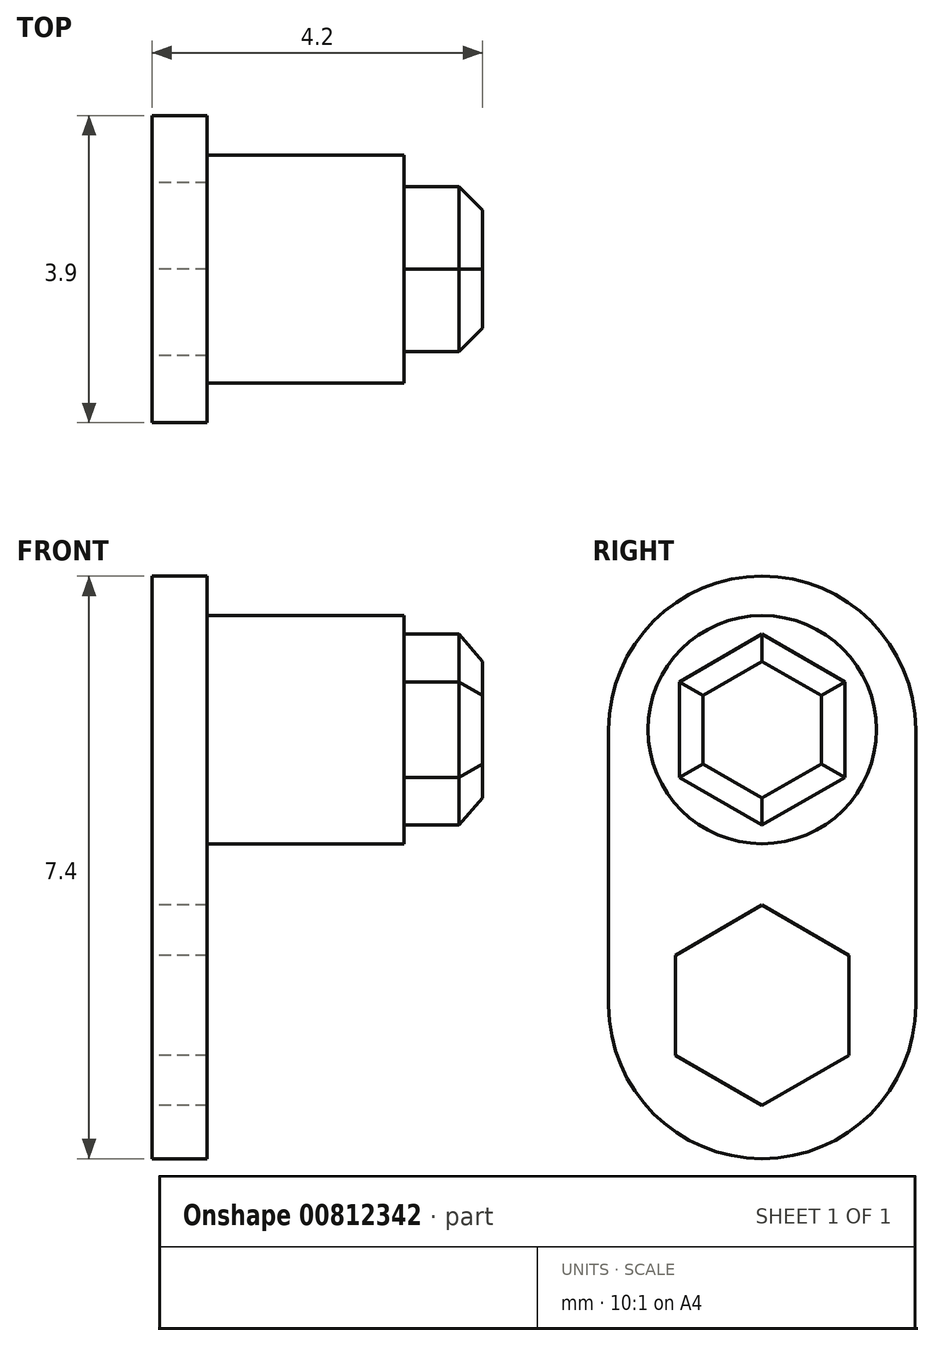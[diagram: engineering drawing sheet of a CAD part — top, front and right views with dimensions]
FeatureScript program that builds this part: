
annotation { "Feature Type Name" : "Feature", "Feature Type Description" : "" }
export const myFeature = defineFeature(function(context is Context, id is Id, definition is map)
    precondition{}
    {
        {
            var Q0;
            Q0=qCreatedBy(makeId("Right.planeOp"),FACE);
            var sketch = newSketch(context, id + "F0", { "sketchPlane" : qUnion([Q0])});
            skLineSegment(sketch, "E0.bottom", {"start": v(1.95, 1.75) * mm, "end": v(-1.95, 1.75) * mm});
            skLineSegment(sketch, "E0.top", {"start": v(1.95, -1.75) * mm, "end": v(-1.95, -1.75) * mm});
            skLineSegment(sketch, "E0.left", {"start": v(1.95, 1.75) * mm, "end": v(1.95, -1.75) * mm});
            skLineSegment(sketch, "E0.right", {"start": v(-1.95, 1.75) * mm, "end": v(-1.95, -1.75) * mm});
            skPoint(sketch, "E0.middle", {"position": v(0, 0) * mm});
            skArc(sketch, "E1", {"start": v(-1.95, 1.75) * mm, "mid": v(0, 3.7) * mm, "end": v(1.95, 1.75) * mm});
            skArc(sketch, "E2", {"start": v(-1.95, -1.75) * mm, "mid": v(0, -3.7) * mm, "end": v(1.95, -1.75) * mm});
            skSolve(sketch);
        }
        {
            var Q0;
            Q0=qSketchRegion(id+"F0",true);
            extrude(context, id + "F1", {"entities" : qUnion([Q0]), "depth" : .7 * mm, "offsetDistance" : 25 * mm});
        }
        {
            var Q0;
            Q0=qCreatedBy(makeId("Right.planeOp"),FACE);
            var sketch = newSketch(context, id + "F2", { "sketchPlane" : qUnion([Q0])});
            skCircle(sketch, "E3", {"center": v(0, 1.75) * mm, "radius": 1.45 * mm});
            skSolve(sketch);
        }
        {
            var Q0;
            Q0=qSketchRegion(id+"F2",true);
            extrude(context, id + "F3", {"entities" : qUnion([Q0]), "operationType" : NewBodyOperationType.ADD, "depth" : 3.2 * mm, "offsetDistance" : 25 * mm});
        }
        {
            var Q0;
            Q0=makeQuery(id+"F3.opExtrude","CAP_FACE",FACE,{"disambiguationData":[OSD([sQuery(id+"F2.wireOp",EDGE,"E3")])],"isStart":false});
            var sketch = newSketch(context, id + "F4", { "sketchPlane" : qUnion([Q0])});
            skCircle(sketch, "E4.cCircle", {"center": v(0, 1.75) * mm, "radius": 1.05 * mm, "construction": true});
            skLineSegment(sketch, "E4.0", {"start": v(1.05, 2.36) * mm, "end": v(1.05, 1.14) * mm});
            skLineSegment(sketch, "E4.1", {"start": v(1.05, 1.14) * mm, "end": v(0, 0.54) * mm});
            skLineSegment(sketch, "E4.2", {"start": v(0, 0.54) * mm, "end": v(-1.05, 1.14) * mm});
            skLineSegment(sketch, "E4.3", {"start": v(-1.05, 1.14) * mm, "end": v(-1.05, 2.36) * mm});
            skLineSegment(sketch, "E4.4", {"start": v(-1.05, 2.36) * mm, "end": v(0, 2.96) * mm});
            skLineSegment(sketch, "E4.5", {"start": v(0, 2.96) * mm, "end": v(1.05, 2.36) * mm});
            skPoint(sketch, "E4.0.midPoint", {"position": v(1.05, 1.75) * mm});
            skSolve(sketch);
        }
        {
            var Q0;
            Q0=qSketchRegion(id+"F4",true);
            extrude(context, id + "F5", {"entities" : qUnion([Q0]), "operationType" : NewBodyOperationType.ADD, "depth" : 1 * mm, "offsetDistance" : 25 * mm});
        }
        {
            var Q0;
            Q0=makeQuery(id+"F5.opExtrude","CAP_EDGE",EDGE,{"disambiguationData":[OSD([sQuery(id+"F4.wireOp",EDGE,"E4.4")])],"isStart":false});
            var Q1;
            Q1=makeQuery(id+"F5.opExtrude","CAP_EDGE",EDGE,{"disambiguationData":[OSD([sQuery(id+"F4.wireOp",EDGE,"E4.5")])],"isStart":false});
            var Q2;
            Q2=makeQuery(id+"F5.opExtrude","CAP_EDGE",EDGE,{"disambiguationData":[OSD([sQuery(id+"F4.wireOp",EDGE,"E4.0")])],"isStart":false});
            var Q3;
            Q3=makeQuery(id+"F5.opExtrude","CAP_EDGE",EDGE,{"disambiguationData":[OSD([sQuery(id+"F4.wireOp",EDGE,"E4.1")])],"isStart":false});
            var Q4;
            Q4=makeQuery(id+"F5.opExtrude","CAP_EDGE",EDGE,{"disambiguationData":[OSD([sQuery(id+"F4.wireOp",EDGE,"E4.2")])],"isStart":false});
            var Q5;
            Q5=makeQuery(id+"F5.opExtrude","CAP_EDGE",EDGE,{"disambiguationData":[OSD([sQuery(id+"F4.wireOp",EDGE,"E4.3")])],"isStart":false});
            chamfer(context, id + "F6", {"entities" : qUnion([Q0, Q1, Q2, Q3, Q4, Q5]), "width" : .3 * mm, "tangentPropagation" : true});
        }
        {
            var Q0;
            Q0=makeQuery(id+"F1.opExtrude","CAP_FACE",FACE,{"disambiguationData":[OSD([sQuery(id+"F0.wireOp",EDGE,"E0.left"),sQuery(id+"F0.wireOp",EDGE,"E0.right"),sQuery(id+"F0.wireOp",EDGE,"E1"),sQuery(id+"F0.wireOp",EDGE,"E2")])],"isStart":true});
            var sketch = newSketch(context, id + "F7", { "sketchPlane" : qUnion([Q0])});
            skCircle(sketch, "E5.cCircle", {"center": v(0, -1.75) * mm, "radius": 1.1 * mm, "construction": true});
            skLineSegment(sketch, "E5.0", {"start": v(1.1, -1.11) * mm, "end": v(1.1, -2.39) * mm});
            skLineSegment(sketch, "E5.1", {"start": v(1.1, -2.39) * mm, "end": v(0, -3.02) * mm});
            skLineSegment(sketch, "E5.2", {"start": v(0, -3.02) * mm, "end": v(-1.1, -2.39) * mm});
            skLineSegment(sketch, "E5.3", {"start": v(-1.1, -2.39) * mm, "end": v(-1.1, -1.11) * mm});
            skLineSegment(sketch, "E5.4", {"start": v(-1.1, -1.11) * mm, "end": v(0, -0.48) * mm});
            skLineSegment(sketch, "E5.5", {"start": v(0, -0.48) * mm, "end": v(1.1, -1.11) * mm});
            skPoint(sketch, "E5.0.midPoint", {"position": v(1.1, -1.75) * mm});
            skSolve(sketch);
        }
        {
            var Q0;
            Q0=qSketchRegion(id+"F7",true);
            extrude(context, id + "F8", {"entities" : qUnion([Q0]), "operationType" : NewBodyOperationType.REMOVE, "endBound" : BoundingType.UP_TO_NEXT, "oppositeDirection" : true, "depth" : 25 * mm, "offsetDistance" : 25 * mm});
        }
    });
